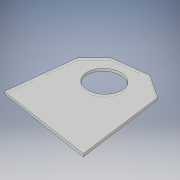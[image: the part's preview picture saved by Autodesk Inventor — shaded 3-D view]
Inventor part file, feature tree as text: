
AUTODESK INVENTOR PART (.ipt)
format: ipt  version: 2019 (Build 230136000, 136)  size: 106,496 bytes
history: native  units: in
note: dims shown in document units (in); Inventor stores cm internally (conversion verified against a paired STEP export)
features: extrude x1, chamfer x1, sketch x1
ambient origin geometry x8: Origin, YZ Plane, XZ Plane, XY Plane, X Axis, Y Axis, Z Axis, Center Point
bodies: Solid1 (feature_tree)
feature tree (3):
  extrude  "Extrusion1"  Depth=0.0625in
  chamfer  "Chamfer1"  Distance=1.0in
  sketch  "Sketch1"  dims[d0=1.0in d1=0.875in d2=1.0in d3=2.25in d4=2.0in d5=0.0625in d6=0.0in d7=0.5in d8=0.125in d9=45.0deg]
